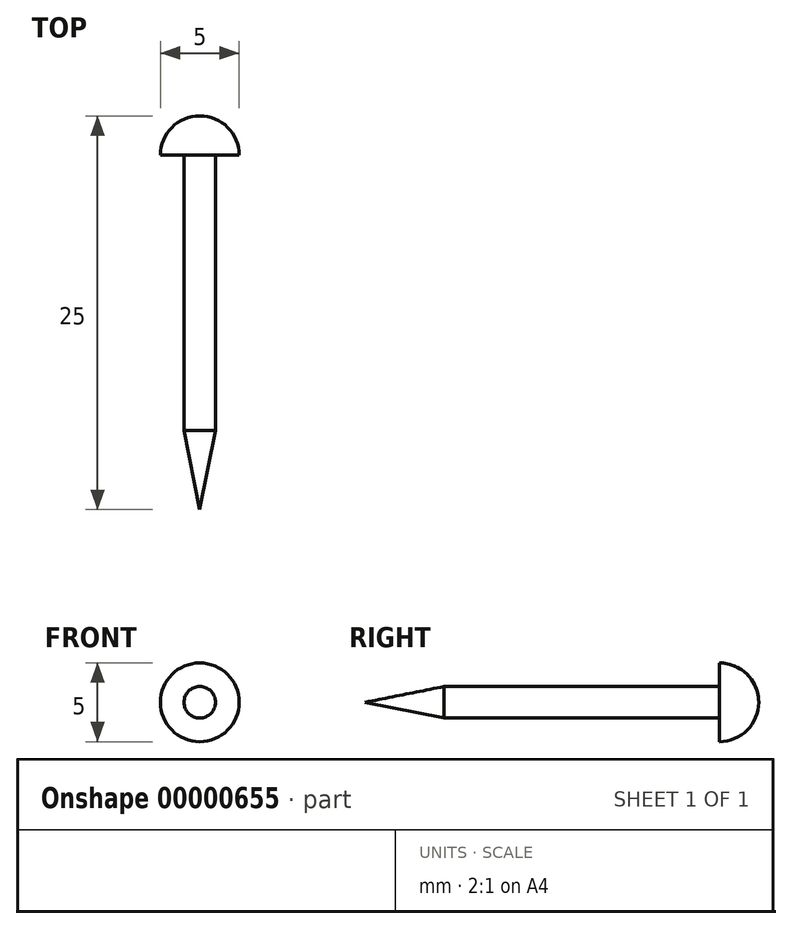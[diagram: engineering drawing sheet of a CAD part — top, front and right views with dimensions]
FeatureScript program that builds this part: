
annotation { "Feature Type Name" : "Feature", "Feature Type Description" : "" }
export const myFeature = defineFeature(function(context is Context, id is Id, definition is map)
    precondition{}
    {
        {
            var Q0;
            Q0=qCreatedBy(makeId("Right.planeOp"),FACE);
            var sketch = newSketch(context, id + "F0", { "sketchPlane" : qUnion([Q0])});
            skLineSegment(sketch, "E0", {"start": v(0, 0) * mm, "end": v(5, 1) * mm});
            skLineSegment(sketch, "E1", {"start": v(5, 1) * mm, "end": v(22.5, 1) * mm});
            skLineSegment(sketch, "E2", {"start": v(22.5, 1) * mm, "end": v(22.5, 2.5) * mm});
            skArc(sketch, "E3", {"start": v(25, 0) * mm, "mid": v(24.27, 1.77) * mm, "end": v(22.5, 2.5) * mm});
            skLineSegment(sketch, "E4", {"start": v(0, 0) * mm, "end": v(-14.94, 0) * mm, "construction": true});
            skLineSegment(sketch, "E5", {"start": v(0, 0) * mm, "end": v(25, 0) * mm});
            skSolve(sketch);
        }
        {
            var Q0;
            Q0=makeQuery(id+"F0.imprint","IMPRINT",FACE,{"disambiguationData":[TD([[makeQuery(id+"F0.imprint","IMPRINT",EDGE,{"derivedFrom":sQuery(id+"F0.wireOp",EDGE,"E0")}),-1.0]])]});
            var Q1;
            Q1=sQuery(id+"F0.wireOp",EDGE,"E5");
            revolve(context, id + "F1", {"entities" : qUnion([Q0]), "axis" : qUnion([Q1]), "revolveType" : RevolveType.FULL});
        }
    });
